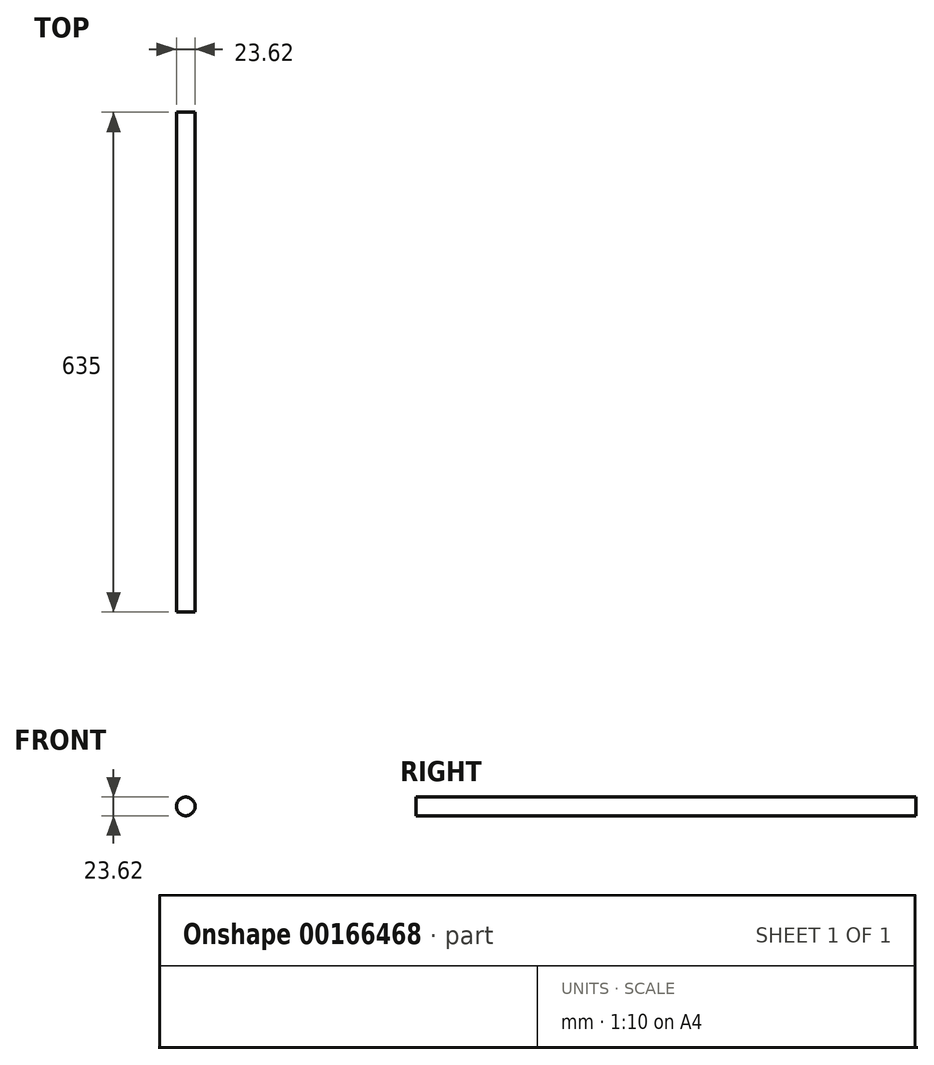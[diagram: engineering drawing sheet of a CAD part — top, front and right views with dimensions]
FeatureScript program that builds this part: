
annotation { "Feature Type Name" : "Feature", "Feature Type Description" : "" }
export const myFeature = defineFeature(function(context is Context, id is Id, definition is map)
    precondition{}
    {
        {
            var Q0;
            Q0=qCreatedBy(makeId("Front.planeOp"),FACE);
            var sketch = newSketch(context, id + "F0", { "sketchPlane" : qUnion([Q0])});
            skCircle(sketch, "E0", {"center": v(0, 0) * mm, "radius": 11.81 * mm});
            skSolve(sketch);
        }
        {
            var Q0;
            Q0 = qSketchRegion(id + "F0", true);
            extrude(context, id + "F1", {"entities" : qUnion([Q0]), "depth" : 635 * mm});
        }
    });
